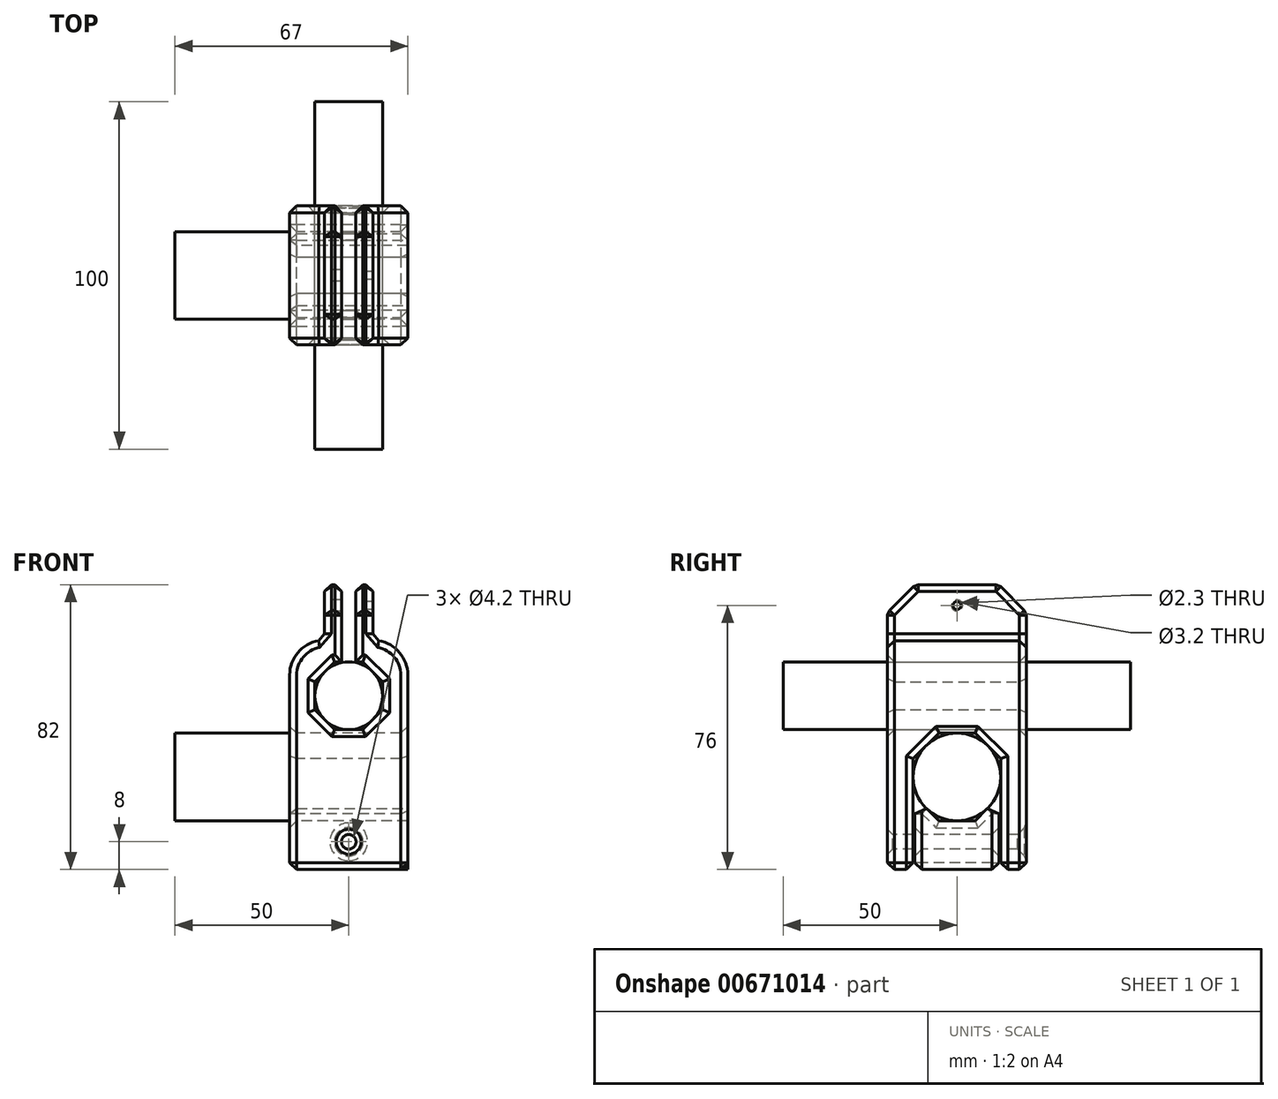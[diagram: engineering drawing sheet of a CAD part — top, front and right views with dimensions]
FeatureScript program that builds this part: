
annotation { "Feature Type Name" : "Feature", "Feature Type Description" : "" }
export const myFeature = defineFeature(function(context is Context, id is Id, definition is map)
    precondition{}
    {
        {
            var Q0;
            Q0=qCreatedBy(makeId("Front.planeOp"),FACE);
            var sketch = newSketch(context, id + "F0", { "sketchPlane" : qUnion([Q0])});
            skCircle(sketch, "E0", {"center": v(0, 0) * mm, "radius": 9.75 * mm});
            skLineSegment(sketch, "E1", {"start": v(-51.67, 0) * mm, "end": v(59.01, 0) * mm, "construction": true});
            skLineSegment(sketch, "E2", {"start": v(0, 51.57) * mm, "end": v(0, -53.7) * mm, "construction": true});
            skSolve(sketch);
        }
        {
            var Q0;
            Q0 = qSketchRegion(id + "F0", true);
            extrude(context, id + "F1", {"entities" : qUnion([Q0]), "endBound" : BoundingType.SYMMETRIC, "depth" : 100 * mm, "offsetDistance" : 25 * mm});
        }
        {
            var Q0;
            Q0=qCreatedBy(makeId("Right.planeOp"),FACE);
            var sketch = newSketch(context, id + "F2", { "sketchPlane" : qUnion([Q0])});
            skCircle(sketch, "E3", {"center": v(0, -23.35) * mm, "radius": 12.6 * mm});
            skLineSegment(sketch, "E4", {"start": v(0, 52.88) * mm, "end": v(0, -60.6) * mm, "construction": true});
            skLineSegment(sketch, "E5", {"start": v(-53.75, -23.35) * mm, "end": v(53.75, -23.35) * mm, "construction": true});
            skLineSegment(sketch, "E6.0", {"start": v(0, -9.75) * mm, "end": v(0, 9.75) * mm, "construction": true});
            skSolve(sketch);
        }
        {
            var Q0;
            Q0 = qSketchRegion(id + "F2", true);
            extrude(context, id + "F3", {"entities" : qUnion([Q0]), "endBound" : BoundingType.SYMMETRIC, "depth" : 100 * mm, "offsetDistance" : 25 * mm});
        }
        {
            var Q0;
            Q0=qCreatedBy(makeId("Front.planeOp"),FACE);
            var sketch = newSketch(context, id + "F4", { "sketchPlane" : qUnion([Q0])});
            skCircle(sketch, "E7.cCircle", {"center": v(0, 0) * mm, "radius": 9.75 * mm, "construction": true});
            skLineSegment(sketch, "E7.0", {"start": v(9.75, 4.04) * mm, "end": v(9.75, -4.04) * mm});
            skLineSegment(sketch, "E7.1", {"start": v(9.75, -4.04) * mm, "end": v(4.04, -9.75) * mm});
            skLineSegment(sketch, "E7.2", {"start": v(4.04, -9.75) * mm, "end": v(-4.04, -9.75) * mm});
            skLineSegment(sketch, "E7.3", {"start": v(-4.04, -9.75) * mm, "end": v(-9.75, -4.04) * mm});
            skLineSegment(sketch, "E7.4", {"start": v(-9.75, -4.04) * mm, "end": v(-9.75, 4.04) * mm});
            skLineSegment(sketch, "E7.5", {"start": v(-9.75, 4.04) * mm, "end": v(-4.04, 9.75) * mm});
            skLineSegment(sketch, "E7.7", {"start": v(4.04, 9.75) * mm, "end": v(9.75, 4.04) * mm});
            skPoint(sketch, "E7.0.midPoint", {"position": v(9.75, 0) * mm});
            skLineSegment(sketch, "E8.top", {"start": v(-17, -50) * mm, "end": v(17, -50) * mm});
            skLineSegment(sketch, "E8.left", {"start": v(-17, 6) * mm, "end": v(-17, -50) * mm});
            skLineSegment(sketch, "E8.right", {"start": v(17, 6) * mm, "end": v(17, -50) * mm});
            skPoint(sketch, "E9.visualSharp", {"position": v(-17, 14) * mm});
            skArc(sketch, "E9.filletArc", {"start": v(-7, 16) * mm, "mid": v(-14.07, 13.07) * mm, "end": v(-17, 6) * mm});
            skPoint(sketch, "E10.visualSharp", {"position": v(17, 14) * mm});
            skArc(sketch, "E10.filletArc", {"start": v(17, 6) * mm, "mid": v(14.07, 13.07) * mm, "end": v(7, 16) * mm});
            skCircle(sketch, "E11", {"center": v(0, -42) * mm, "radius": 1.6 * mm});
            skCircle(sketch, "E12", {"center": v(0, -42) * mm, "radius": 2.1 * mm});
            skLineSegment(sketch, "E13.bottom", {"start": v(2, 32) * mm, "end": v(7, 32) * mm});
            skLineSegment(sketch, "E13.top", {"start": v(2, 9.75) * mm, "end": v(4.04, 9.75) * mm});
            skLineSegment(sketch, "E13.left", {"start": v(2, 32) * mm, "end": v(2, 9.75) * mm});
            skLineSegment(sketch, "E13.right", {"start": v(7, 32) * mm, "end": v(7, 16) * mm});
            skLineSegment(sketch, "E14.MirrorCS", {"start": v(-7, 32) * mm, "end": v(-7, 16) * mm});
            skLineSegment(sketch, "E15.MirrorCS", {"start": v(-2, 9.75) * mm, "end": v(-4.04, 9.75) * mm});
            skLineSegment(sketch, "E16.MirrorCS", {"start": v(-2, 32) * mm, "end": v(-7, 32) * mm});
            skLineSegment(sketch, "E17.MirrorCS", {"start": v(-2, 32) * mm, "end": v(-2, 9.75) * mm});
            skSolve(sketch);
        }
        {
            var Q0;
            Q0=makeQuery(id+"F4.imprint","IMPRINT",FACE,{"disambiguationData":[TD([[makeQuery(id+"F4.imprint","IMPRINT",EDGE,{"derivedFrom":sQuery(id+"F4.wireOp",EDGE,"E7.0")}),1.0]])]});
            var Q1;
            Q1=makeQuery(id+"F4.imprint","IMPRINT",FACE,{"disambiguationData":[TD([[makeQuery(id+"F4.imprint","IMPRINT",EDGE,{"derivedFrom":sQuery(id+"F4.wireOp",EDGE,"E11")}),-1.0]])]});
            extrude(context, id + "F5", {"entities" : qUnion([Q0, Q1]), "endBound" : BoundingType.SYMMETRIC, "depth" : 40 * mm, "offsetDistance" : 25 * mm});
        }
        {
            var Q0;
            Q0=makeQuery(id+"F5.opExtrude","SWEPT_FACE",FACE,{"disambiguationData":[OSD([sQuery(id+"F4.wireOp",EDGE,"E8.left")])]});
            var sketch = newSketch(context, id + "F6", { "sketchPlane" : qUnion([Q0])});
            skCircle(sketch, "E18.cCircle", {"center": v(0, -23.35) * mm, "radius": 12.6 * mm, "construction": true});
            skLineSegment(sketch, "E18.0", {"start": v(12.1, -29.07) * mm, "end": v(5.22, -35.95) * mm});
            skLineSegment(sketch, "E18.1", {"start": v(5.22, -35.95) * mm, "end": v(-5.22, -35.95) * mm});
            skLineSegment(sketch, "E18.2", {"start": v(-5.22, -35.95) * mm, "end": v(-12.1, -29.07) * mm});
            skLineSegment(sketch, "E18.3", {"start": v(-12.6, -28.57) * mm, "end": v(-12.6, -18.13) * mm});
            skLineSegment(sketch, "E18.4", {"start": v(-12.6, -18.13) * mm, "end": v(-5.22, -10.75) * mm});
            skLineSegment(sketch, "E18.5", {"start": v(-5.22, -10.75) * mm, "end": v(5.22, -10.75) * mm});
            skLineSegment(sketch, "E18.6", {"start": v(5.22, -10.75) * mm, "end": v(12.6, -18.13) * mm});
            skLineSegment(sketch, "E18.7", {"start": v(12.6, -18.13) * mm, "end": v(12.6, -28.57) * mm});
            skPoint(sketch, "E18.0.midPoint", {"position": v(8.9, -32.26) * mm});
            skLineSegment(sketch, "E19", {"start": v(-12.6, -28.57) * mm, "end": v(-12.6, -50) * mm});
            skLineSegment(sketch, "E20", {"start": v(-12.6, -50) * mm, "end": v(12.6, -50) * mm});
            skLineSegment(sketch, "E21", {"start": v(12.6, -50) * mm, "end": v(12.6, -28.57) * mm});
            skLineSegment(sketch, "E22", {"start": v(12.1, -50) * mm, "end": v(12.1, -29.07) * mm});
            skLineSegment(sketch, "E23", {"start": v(-12.1, -50) * mm, "end": v(-12.1, -29.07) * mm});
            skCircle(sketch, "E24", {"center": v(0, 26) * mm, "radius": 1.6 * mm});
            skCircle(sketch, "E25", {"center": v(0, 26) * mm, "radius": 1.15 * mm});
            skLineSegment(sketch, "E26", {"start": v(12, 32) * mm, "end": v(20, 32) * mm});
            skLineSegment(sketch, "E27", {"start": v(20, 32) * mm, "end": v(20, 24) * mm});
            skLineSegment(sketch, "E28", {"start": v(20, 24) * mm, "end": v(12, 32) * mm});
            skLineSegment(sketch, "E29.MirrorCS", {"start": v(-20, 24) * mm, "end": v(-12, 32) * mm});
            skLineSegment(sketch, "E30.MirrorCS", {"start": v(-20, 32) * mm, "end": v(-20, 24) * mm});
            skLineSegment(sketch, "E31.MirrorCS", {"start": v(-12, 32) * mm, "end": v(-20, 32) * mm});
            skSolve(sketch);
        }
        {
            var Q0;
            Q0=makeQuery(id+"F6.imprint","IMPRINT",FACE,{"disambiguationData":[TD([[makeQuery(id+"F6.imprint","IMPRINT",EDGE,{"derivedFrom":sQuery(id+"F6.wireOp",EDGE,"E18.0")}),-1.0]])]});
            var Q1;
            Q1=makeQuery(id+"F6.imprint","IMPRINT",FACE,{"disambiguationData":[TD([[makeQuery(id+"F6.imprint","IMPRINT",EDGE,{"derivedFrom":sQuery(id+"F6.wireOp",EDGE,"E29.MirrorCS")}),1.0]])]});
            var Q2;
            Q2=makeQuery(id+"F6.imprint","IMPRINT",FACE,{"disambiguationData":[TD([[makeQuery(id+"F6.imprint","IMPRINT",EDGE,{"derivedFrom":sQuery(id+"F6.wireOp",EDGE,"E26")}),-1.0]])]});
            var Q3;
            Q3=makeQuery(id+"F6.imprint","IMPRINT",FACE,{"disambiguationData":[TD([[makeQuery(id+"F6.imprint","IMPRINT",EDGE,{"derivedFrom":sQuery(id+"F6.wireOp",EDGE,"E25")}),1.0]])]});
            var Q4;
            Q4=makeQuery(id+"F6.imprint","IMPRINT",FACE,{"disambiguationData":[TD([[makeQuery(id+"F6.imprint","IMPRINT",EDGE,{"derivedFrom":sQuery(id+"F6.wireOp",EDGE,"E18.0")}),1.0]])]});
            extrude(context, id + "F7", {"entities" : qUnion([Q0, Q1, Q2, Q3, Q4]), "operationType" : NewBodyOperationType.REMOVE, "endBound" : BoundingType.THROUGH_ALL, "oppositeDirection" : true, "depth" : 25 * mm, "offsetDistance" : 25 * mm});
        }
        {
            var Q0;
            Q0=makeQuery(id+"F6.imprint","IMPRINT",FACE,{"disambiguationData":[TD([[makeQuery(id+"F6.imprint","IMPRINT",EDGE,{"derivedFrom":sQuery(id+"F6.wireOp",EDGE,"E24")}),1.0]])]});
            var Q1;
            Q1=makeQuery(id+"F5.opExtrude","SWEPT_FACE",FACE,{"disambiguationData":[OSD([sQuery(id+"F4.wireOp",EDGE,"E17.MirrorCS")])]});
            extrude(context, id + "F8", {"entities" : qUnion([Q0]), "operationType" : NewBodyOperationType.REMOVE, "endBound" : BoundingType.UP_TO_SURFACE, "oppositeDirection" : true, "depth" : 25 * mm, "endBoundEntityFace" : qUnion([Q1]), "offsetDistance" : 25 * mm});
        }
        {
            var Q0;
            Q0=makeQuery(id+"F4.imprint","IMPRINT",FACE,{"disambiguationData":[TD([[makeQuery(id+"F4.imprint","IMPRINT",EDGE,{"derivedFrom":sQuery(id+"F4.wireOp",EDGE,"E11")}),-1.0]])]});
            extrude(context, id + "F9", {"entities" : qUnion([Q0]), "operationType" : NewBodyOperationType.REMOVE, "endBound" : BoundingType.THROUGH_ALL, "oppositeDirection" : true, "depth" : 25 * mm, "offsetDistance" : 25 * mm});
        }
        {
            var Q0;
            Q0=makeQuery(id+"F9.boolean.opBoolean","INTERSECT",EDGE,{"derivedFrom":[makeQuery(id+"F5.opExtrude","CAP_FACE",FACE,{"disambiguationData":[OSD([sQuery(id+"F4.wireOp",EDGE,"E7.0"),sQuery(id+"F4.wireOp",EDGE,"E7.1"),sQuery(id+"F4.wireOp",EDGE,"E7.2"),sQuery(id+"F4.wireOp",EDGE,"E7.3"),sQuery(id+"F4.wireOp",EDGE,"E7.4"),sQuery(id+"F4.wireOp",EDGE,"E7.5"),sQuery(id+"F4.wireOp",EDGE,"E7.6"),sQuery(id+"F4.wireOp",EDGE,"E7.7"),sQuery(id+"F4.wireOp",EDGE,"E8.bottom"),sQuery(id+"F4.wireOp",EDGE,"E8.top"),sQuery(id+"F4.wireOp",EDGE,"E8.left"),sQuery(id+"F4.wireOp",EDGE,"E8.right"),sQuery(id+"F4.wireOp",EDGE,"E9.filletArc"),sQuery(id+"F4.wireOp",EDGE,"E10.filletArc"),sQuery(id+"F4.wireOp",EDGE,"E11")])],"isStart":true}),makeQuery(id+"F9.opExtrude","SWEPT_FACE",FACE,{"disambiguationData":[OSD([sQuery(id+"F4.wireOp",EDGE,"E12")])]})]});
            chamfer(context, id + "F10", {"entities" : qUnion([Q0]), "width" : 2.5 * mm, "tangentPropagation" : true});
        }
        {
            var Q0;
            Q0=makeQuery(id+"F5.opExtrude","SWEPT_FACE",FACE,{"disambiguationData":[OSD([sQuery(id+"F4.wireOp",EDGE,"E8.right")])]});
            var Q1;
            {var subQ2=sQuery(id+"F4.wireOp",EDGE,"E8.top");Q1=makeQuery(id+"F7.boolean.opBoolean","SPLIT",FACE,{"disambiguationData":[TD([makeQuery(id+"F7.opExtrude","SWEPT_FACE",FACE,{"disambiguationData":[OSD([sQuery(id+"F6.wireOp",EDGE,"E18.7"),sQuery(id+"F6.wireOp",EDGE,"E21")])]})])],"derivedFrom":makeQuery(id+"F5.opExtrude","SWEPT_FACE",FACE,{"disambiguationData":[OSD([subQ2])]})});}
            var Q2;
            {var subQ2=sQuery(id+"F4.wireOp",EDGE,"E8.top");Q2=makeQuery(id+"F7.boolean.opBoolean","SPLIT",FACE,{"disambiguationData":[TD([makeQuery(id+"F7.opExtrude","SWEPT_FACE",FACE,{"disambiguationData":[OSD([sQuery(id+"F6.wireOp",EDGE,"E18.3"),sQuery(id+"F6.wireOp",EDGE,"E19")])]})])],"derivedFrom":makeQuery(id+"F5.opExtrude","SWEPT_FACE",FACE,{"disambiguationData":[OSD([subQ2])]})});}
            var Q3;
            Q3=makeQuery(id+"F5.opExtrude","CAP_FACE",FACE,{"disambiguationData":[OSD([sQuery(id+"F4.wireOp",EDGE,"E7.0"),sQuery(id+"F4.wireOp",EDGE,"E7.1"),sQuery(id+"F4.wireOp",EDGE,"E7.2"),sQuery(id+"F4.wireOp",EDGE,"E7.3"),sQuery(id+"F4.wireOp",EDGE,"E7.4"),sQuery(id+"F4.wireOp",EDGE,"E7.5"),sQuery(id+"F4.wireOp",EDGE,"E7.6"),sQuery(id+"F4.wireOp",EDGE,"E7.7"),sQuery(id+"F4.wireOp",EDGE,"E8.bottom"),sQuery(id+"F4.wireOp",EDGE,"E8.top"),sQuery(id+"F4.wireOp",EDGE,"E8.left"),sQuery(id+"F4.wireOp",EDGE,"E8.right"),sQuery(id+"F4.wireOp",EDGE,"E9.filletArc"),sQuery(id+"F4.wireOp",EDGE,"E10.filletArc"),sQuery(id+"F4.wireOp",EDGE,"E11")])],"isStart":true});
            var Q4;
            Q4=makeQuery(id+"F5.opExtrude","CAP_FACE",FACE,{"disambiguationData":[OSD([sQuery(id+"F4.wireOp",EDGE,"E7.0"),sQuery(id+"F4.wireOp",EDGE,"E7.1"),sQuery(id+"F4.wireOp",EDGE,"E7.2"),sQuery(id+"F4.wireOp",EDGE,"E7.3"),sQuery(id+"F4.wireOp",EDGE,"E7.4"),sQuery(id+"F4.wireOp",EDGE,"E7.5"),sQuery(id+"F4.wireOp",EDGE,"E7.6"),sQuery(id+"F4.wireOp",EDGE,"E7.7"),sQuery(id+"F4.wireOp",EDGE,"E8.bottom"),sQuery(id+"F4.wireOp",EDGE,"E8.top"),sQuery(id+"F4.wireOp",EDGE,"E8.left"),sQuery(id+"F4.wireOp",EDGE,"E8.right"),sQuery(id+"F4.wireOp",EDGE,"E9.filletArc"),sQuery(id+"F4.wireOp",EDGE,"E10.filletArc"),sQuery(id+"F4.wireOp",EDGE,"E11")])],"isStart":false});
            var Q5;
            Q5=makeQuery(id+"F5.opExtrude","SWEPT_FACE",FACE,{"disambiguationData":[OSD([sQuery(id+"F4.wireOp",EDGE,"E8.left")])]});
            var Q6;
            Q6=makeQuery(id+"F5.opExtrude","SWEPT_FACE",FACE,{"disambiguationData":[OSD([sQuery(id+"F4.wireOp",EDGE,"E16.MirrorCS")])]});
            var Q7;
            Q7=makeQuery(id+"F5.opExtrude","SWEPT_FACE",FACE,{"disambiguationData":[OSD([sQuery(id+"F4.wireOp",EDGE,"E13.bottom")])]});
            var Q8;
            Q8=makeQuery(id+"F5.opExtrude","SWEPT_EDGE",EDGE,{"disambiguationData":[OSD([sQuery(id+"F4.wireOp",EDGE,"E9.filletArc"),sQuery(id+"F4.wireOp",EDGE,"E14.MirrorCS")])]});
            var Q9;
            Q9=makeQuery(id+"F5.opExtrude","SWEPT_EDGE",EDGE,{"disambiguationData":[OSD([sQuery(id+"F4.wireOp",EDGE,"E10.filletArc"),sQuery(id+"F4.wireOp",EDGE,"E13.right")])]});
            var Q10;
            {var subQ2=sQuery(id+"F4.wireOp",EDGE,"E14.MirrorCS");Q10=makeQuery(id+"F7.boolean.opBoolean","COPY",FACE,{"disambiguationData":[TD([makeQuery(id+"F5.opExtrude","SWEPT_FACE",FACE,{"disambiguationData":[OSD([subQ2])]})])],"derivedFrom":makeQuery(id+"F7.opExtrude","SWEPT_FACE",FACE,{"disambiguationData":[OSD([sQuery(id+"F6.wireOp",EDGE,"E28")])]})});}
            var Q11;
            {var subQ2=sQuery(id+"F4.wireOp",EDGE,"E13.bottom");Q11=makeQuery(id+"F7.boolean.opBoolean","COPY",FACE,{"disambiguationData":[TD([makeQuery(id+"F5.opExtrude","SWEPT_FACE",FACE,{"disambiguationData":[OSD([subQ2])]})])],"derivedFrom":makeQuery(id+"F7.opExtrude","SWEPT_FACE",FACE,{"disambiguationData":[OSD([sQuery(id+"F6.wireOp",EDGE,"E28")])]})});}
            var Q12;
            {var subQ2=sQuery(id+"F4.wireOp",EDGE,"E14.MirrorCS");Q12=makeQuery(id+"F7.boolean.opBoolean","COPY",FACE,{"disambiguationData":[TD([makeQuery(id+"F5.opExtrude","SWEPT_FACE",FACE,{"disambiguationData":[OSD([subQ2])]})])],"derivedFrom":makeQuery(id+"F7.opExtrude","SWEPT_FACE",FACE,{"disambiguationData":[OSD([sQuery(id+"F6.wireOp",EDGE,"E29.MirrorCS")])]})});}
            var Q13;
            {var subQ2=sQuery(id+"F4.wireOp",EDGE,"E13.bottom");Q13=makeQuery(id+"F7.boolean.opBoolean","COPY",FACE,{"disambiguationData":[TD([makeQuery(id+"F5.opExtrude","SWEPT_FACE",FACE,{"disambiguationData":[OSD([subQ2])]})])],"derivedFrom":makeQuery(id+"F7.opExtrude","SWEPT_FACE",FACE,{"disambiguationData":[OSD([sQuery(id+"F6.wireOp",EDGE,"E29.MirrorCS")])]})});}
            chamfer(context, id + "F11", {"entities" : qUnion([Q0, Q1, Q2, Q3, Q4, Q5, Q6, Q7, Q8, Q9, Q10, Q11, Q12, Q13]), "width" : 2 * mm, "tangentPropagation" : true});
        }
        {
            var Q0;
            Q0=makeQuery(id+"F6.imprint","IMPRINT",FACE,{"disambiguationData":[TD([[makeQuery(id+"F6.imprint","IMPRINT",EDGE,{"derivedFrom":sQuery(id+"F6.wireOp",EDGE,"E18.0")}),1.0]])]});
            var Q1;
            Q1=makeQuery(id+"F5.opExtrude","SWEPT_FACE",FACE,{"disambiguationData":[OSD([sQuery(id+"F4.wireOp",EDGE,"E8.right")])]});
            extrude(context, id + "F12", {"entities" : qUnion([Q0]), "endBound" : BoundingType.UP_TO_SURFACE, "oppositeDirection" : true, "depth" : 25 * mm, "endBoundEntityFace" : qUnion([Q1]), "offsetDistance" : 25 * mm});
        }
        {
            var Q0;
            Q0=makeQuery(id+"F4.imprint","IMPRINT",FACE,{"disambiguationData":[TD([[makeQuery(id+"F4.imprint","IMPRINT",EDGE,{"derivedFrom":sQuery(id+"F4.wireOp",EDGE,"E11")}),-1.0]])]});
            var Q1;
            Q1=makeQuery(id+"F4.imprint","IMPRINT",FACE,{"disambiguationData":[TD([[makeQuery(id+"F4.imprint","IMPRINT",EDGE,{"derivedFrom":sQuery(id+"F4.wireOp",EDGE,"E11")}),1.0]])]});
            var Q2;
            Q2=sQuery(id+"F4.wireOp",EDGE,"E12");
            extrude(context, id + "F13", {"entities" : qUnion([Q0, Q1]), "operationType" : NewBodyOperationType.REMOVE, "surfaceEntities" : qUnion([Q2]), "endBound" : BoundingType.SYMMETRIC, "oppositeDirection" : true, "depth" : 100 * mm, "offsetDistance" : 25 * mm});
        }
        {
            var Q0;
            Q0=makeQuery(id+"F12.opExtrude","CAP_FACE",FACE,{"disambiguationData":[OSD([sQuery(id+"F4.wireOp",EDGE,"E8.right")])],"isStart":false});
            var Q1;
            Q1=makeQuery(id+"F12.opExtrude","CAP_FACE",FACE,{"disambiguationData":[OSD([sQuery(id+"F6.wireOp",EDGE,"E18.0"),sQuery(id+"F6.wireOp",EDGE,"E18.1"),sQuery(id+"F6.wireOp",EDGE,"E18.2"),sQuery(id+"F6.wireOp",EDGE,"E19"),sQuery(id+"F6.wireOp",EDGE,"E20"),sQuery(id+"F6.wireOp",EDGE,"E21")])],"isStart":true});
            var Q2;
            Q2=makeQuery(id+"F12.opExtrude","SWEPT_FACE",FACE,{"disambiguationData":[OSD([sQuery(id+"F6.wireOp",EDGE,"E21")])]});
            var Q3;
            Q3=makeQuery(id+"F12.opExtrude","SWEPT_FACE",FACE,{"disambiguationData":[OSD([sQuery(id+"F6.wireOp",EDGE,"E19")])]});
            var Q4;
            Q4=makeQuery(id+"F12.opExtrude","SWEPT_FACE",FACE,{"disambiguationData":[OSD([sQuery(id+"F6.wireOp",EDGE,"E22")])]});
            var Q5;
            Q5=makeQuery(id+"F12.opExtrude","SWEPT_FACE",FACE,{"disambiguationData":[OSD([sQuery(id+"F6.wireOp",EDGE,"E23")])]});
            chamfer(context, id + "F14", {"entities" : qUnion([Q0, Q1, Q2, Q3, Q4, Q5]), "width" : 2 * mm, "tangentPropagation" : true});
        }
    });
